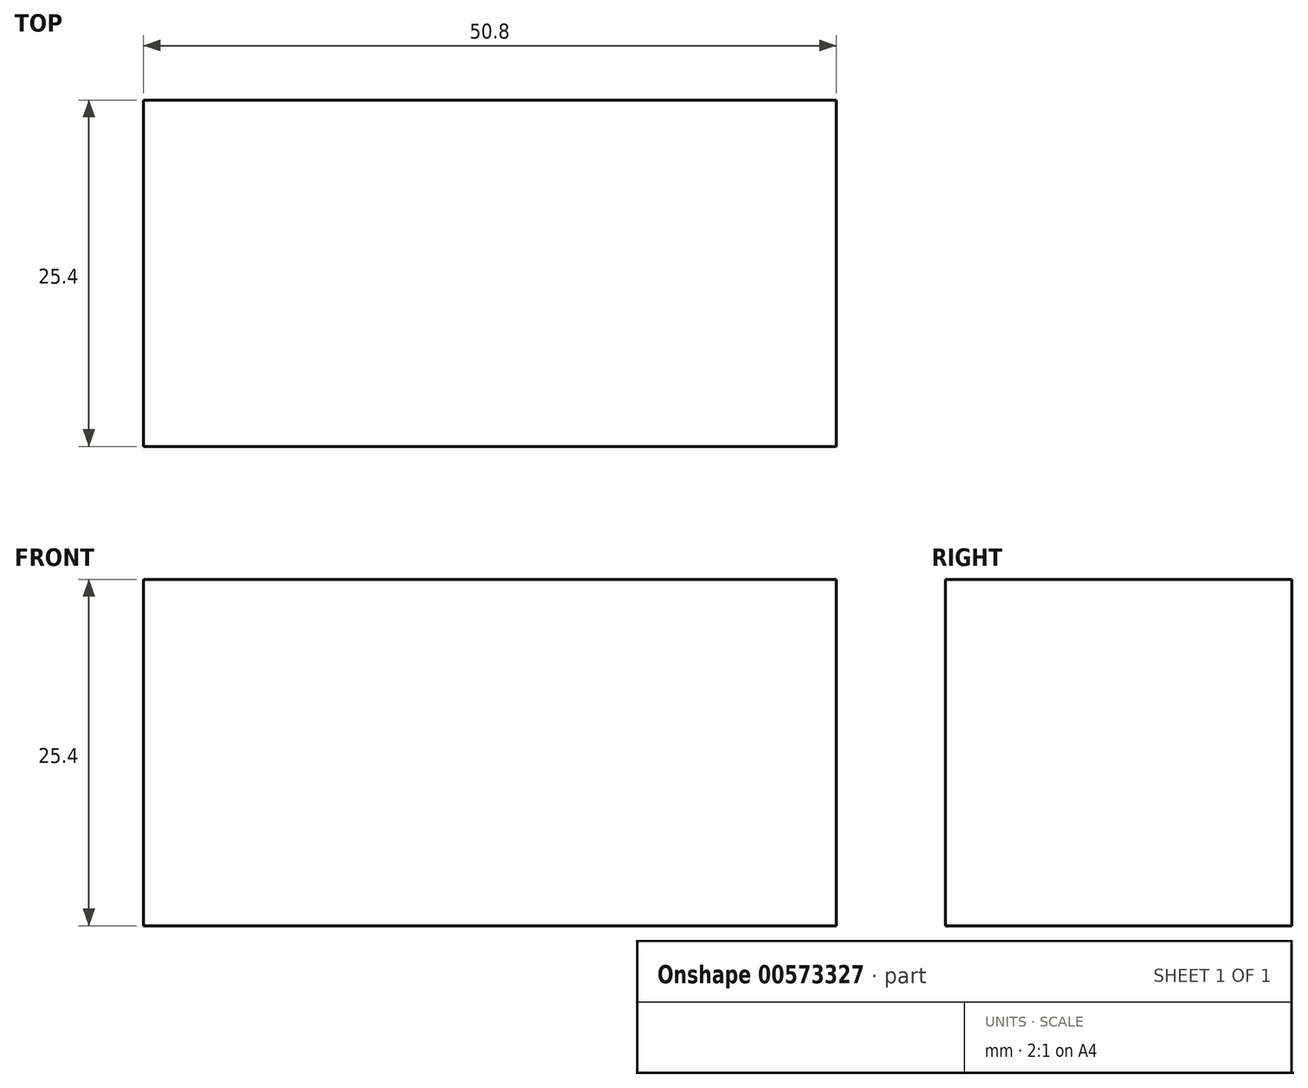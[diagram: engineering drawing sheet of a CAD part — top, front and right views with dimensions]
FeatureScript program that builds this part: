
annotation { "Feature Type Name" : "Feature", "Feature Type Description" : "" }
export const myFeature = defineFeature(function(context is Context, id is Id, definition is map)
    precondition{}
    {
        {
            var Q0;
            Q0=qCreatedBy(makeId("Top.planeOp"),FACE);
            var sketch = newSketch(context, id + "F0", { "sketchPlane" : qUnion([Q0])});
            skLineSegment(sketch, "E0.bottom", {"start": v(-25.4, 12.7) * mm, "end": v(25.4, 12.7) * mm});
            skLineSegment(sketch, "E0.top", {"start": v(-25.4, -12.7) * mm, "end": v(25.4, -12.7) * mm});
            skLineSegment(sketch, "E0.left", {"start": v(-25.4, 12.7) * mm, "end": v(-25.4, -12.7) * mm});
            skLineSegment(sketch, "E0.right", {"start": v(25.4, 12.7) * mm, "end": v(25.4, -12.7) * mm});
            skPoint(sketch, "E0.middle", {"position": v(0, 0) * mm});
            skSolve(sketch);
        }
        {
            var Q0;
            Q0=makeQuery(id+"F0.imprint","IMPRINT",FACE,{"disambiguationData":[TD([[makeQuery(id+"F0.imprint","IMPRINT",EDGE,{"derivedFrom":sQuery(id+"F0.wireOp",EDGE,"E0.bottom")}),-1.0]])]});
            extrude(context, id + "F1", {"entities" : qUnion([Q0]), "depth" : 25.4 * mm, "offsetDistance" : 25.4 * mm});
        }
    });
